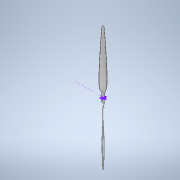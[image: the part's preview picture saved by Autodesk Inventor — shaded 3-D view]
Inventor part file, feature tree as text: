
AUTODESK INVENTOR PART (.ipt)
format: ipt  version: 2022 (Build 260153000, 153)  size: 1,575,936 bytes
history: native  units: mm
features: sketch x5, sweep x2
ambient origin geometry x8: Origin, YZ Plane, XZ Plane, XY Plane, X Axis, Y Axis, Z Axis, Center Point
bodies: Solid1 (feature_tree)
feature tree (7):
  sketch  "Sketch1"  dims[d0=330.0mm d1=90.0deg]
  sweep  "Sweep1"
  sweep  "Sweep2"
  sketch  "Sketch2"  dims[d6=0.0mm d7=0.0mm d8=330.0mm]
  sketch  "3D Sketch1"
  sketch  "Sketch3"  dims[d9=90.0deg d10=0.0mm d11=0.0mm]
  sketch  "3D Sketch2"
